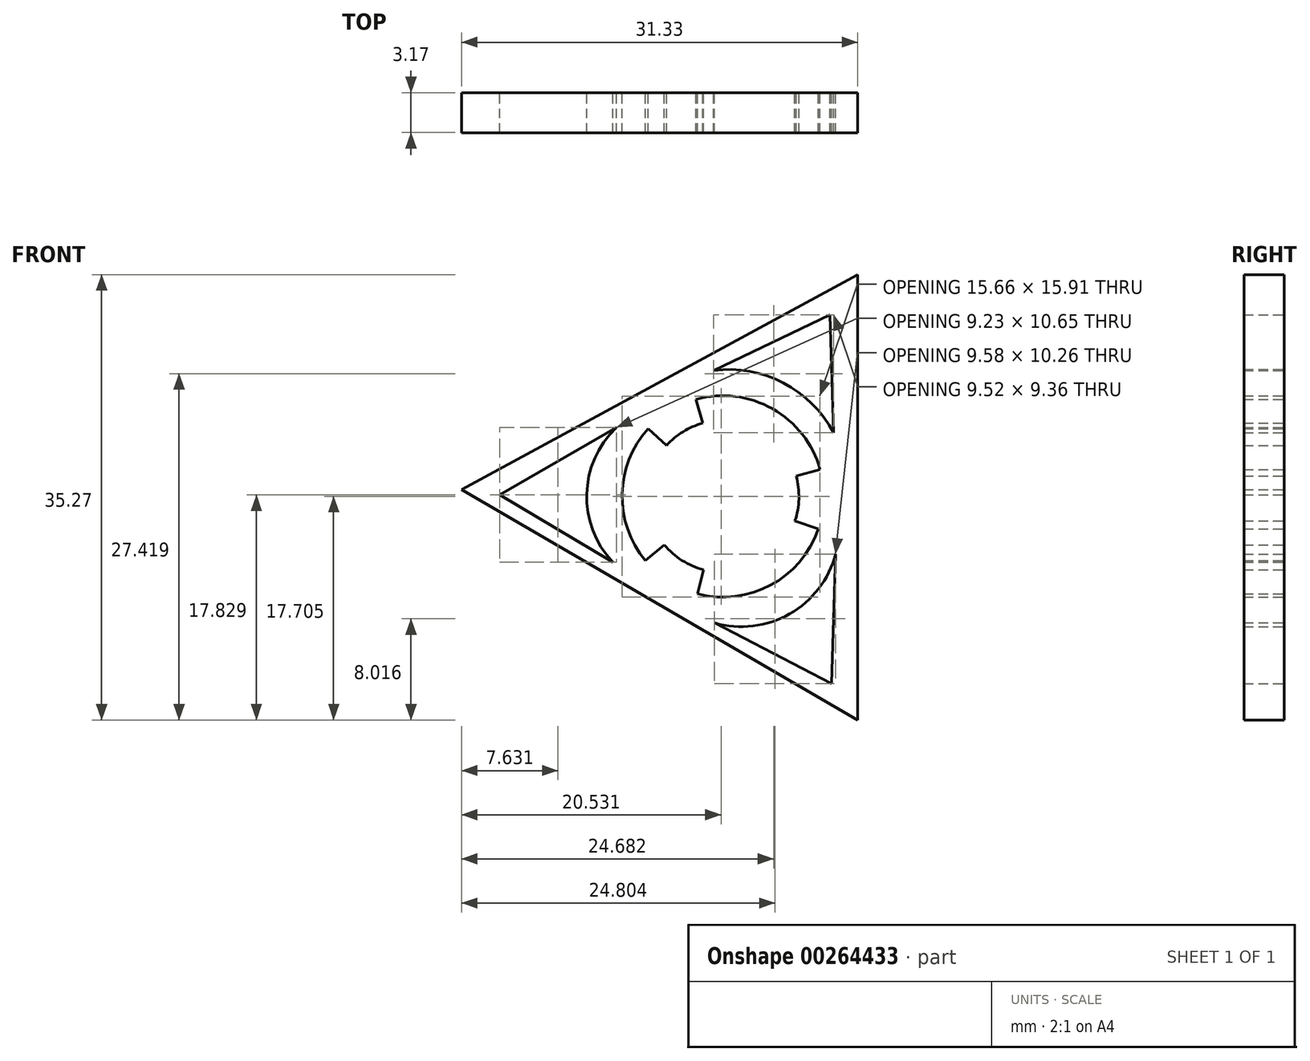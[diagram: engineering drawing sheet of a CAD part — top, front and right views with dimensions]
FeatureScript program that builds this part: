
annotation { "Feature Type Name" : "Feature", "Feature Type Description" : "" }
export const myFeature = defineFeature(function(context is Context, id is Id, definition is map)
    precondition{}
    {
        {
            var Q0;
            Q0=qCreatedBy(makeId("Front.planeOp"),FACE);
            var sketch = newSketch(context, id + "F0", { "sketchPlane" : qUnion([Q0])});
            skArc(sketch, "E0", {"start": v(-88.94, -5.84) * mm, "mid": v(-91, -11.02) * mm, "end": v(-89.17, -16.28) * mm});
            skArc(sketch, "E1", {"start": v(-83.69, -21.2) * mm, "mid": v(-77.75, -20.5) * mm, "end": v(-74.1, -15.76) * mm});
            skArc(sketch, "E2", {"start": v(-74.26, -6.16) * mm, "mid": v(-78.25, -2.2) * mm, "end": v(-83.78, -1.21) * mm});
            skLineSegment(sketch, "E3", {"start": v(-83.78, -1.21) * mm, "end": v(-74.55, 3.2) * mm});
            skLineSegment(sketch, "E4", {"start": v(-74.26, -6.16) * mm, "end": v(-74.55, 3.2) * mm});
            skLineSegment(sketch, "E5", {"start": v(-83.69, -21.2) * mm, "end": v(-74.43, -26.01) * mm});
            skLineSegment(sketch, "E6", {"start": v(-74.43, -26.01) * mm, "end": v(-74.1, -15.76) * mm});
            skArc(sketch, "E7", {"start": v(-91.46, -5.74) * mm, "mid": v(-93.8, -11.01) * mm, "end": v(-91.74, -16.4) * mm});
            skLineSegment(sketch, "E8", {"start": v(-91.46, -5.74) * mm, "end": v(-100.68, -11.07) * mm});
            skLineSegment(sketch, "E9", {"start": v(-91.74, -16.4) * mm, "end": v(-100.68, -11.07) * mm});
            skCircle(sketch, "E10", {"center": v(-83.03, -11.2) * mm, "radius": 6.01 * mm});
            skLineSegment(sketch, "E11", {"start": v(-83.03, -11.2) * mm, "end": v(-89.17, -16.28) * mm});
            skLineSegment(sketch, "E12", {"start": v(-83.03, -11.2) * mm, "end": v(-85.05, -18.9) * mm});
            skLineSegment(sketch, "E13", {"start": v(-83.03, -11.2) * mm, "end": v(-88.94, -5.84) * mm});
            skLineSegment(sketch, "E14", {"start": v(-83.03, -11.2) * mm, "end": v(-85.15, -3.5) * mm});
            skLineSegment(sketch, "E15", {"start": v(-83.03, -11.2) * mm, "end": v(-75.34, -9.07) * mm});
            skLineSegment(sketch, "E16", {"start": v(-83.03, -11.2) * mm, "end": v(-75.48, -13.78) * mm});
            skArc(sketch, "E17.trimOffspring", {"start": v(-75.34, -9.07) * mm, "mid": v(-79.1, -4.25) * mm, "end": v(-85.15, -3.5) * mm});
            skArc(sketch, "E18.trimOffspring", {"start": v(-85.05, -18.9) * mm, "mid": v(-79.26, -18.22) * mm, "end": v(-75.48, -13.78) * mm});
            skLineSegment(sketch, "E19", {"start": v(-103.7, -10.64) * mm, "end": v(-72.37, 6.37) * mm});
            skLineSegment(sketch, "E20", {"start": v(-103.7, -10.64) * mm, "end": v(-72.37, -28.9) * mm});
            skLineSegment(sketch, "E21", {"start": v(-72.37, -28.9) * mm, "end": v(-72.37, 6.37) * mm});
            skSolve(sketch);
        }
        {
            var Q0;
            Q0 = qSketchRegion(id + "F0", true);
            extrude(context, id + "F1", {"entities" : qUnion([Q0]), "depth" : 3.17 * mm});
        }
    });
